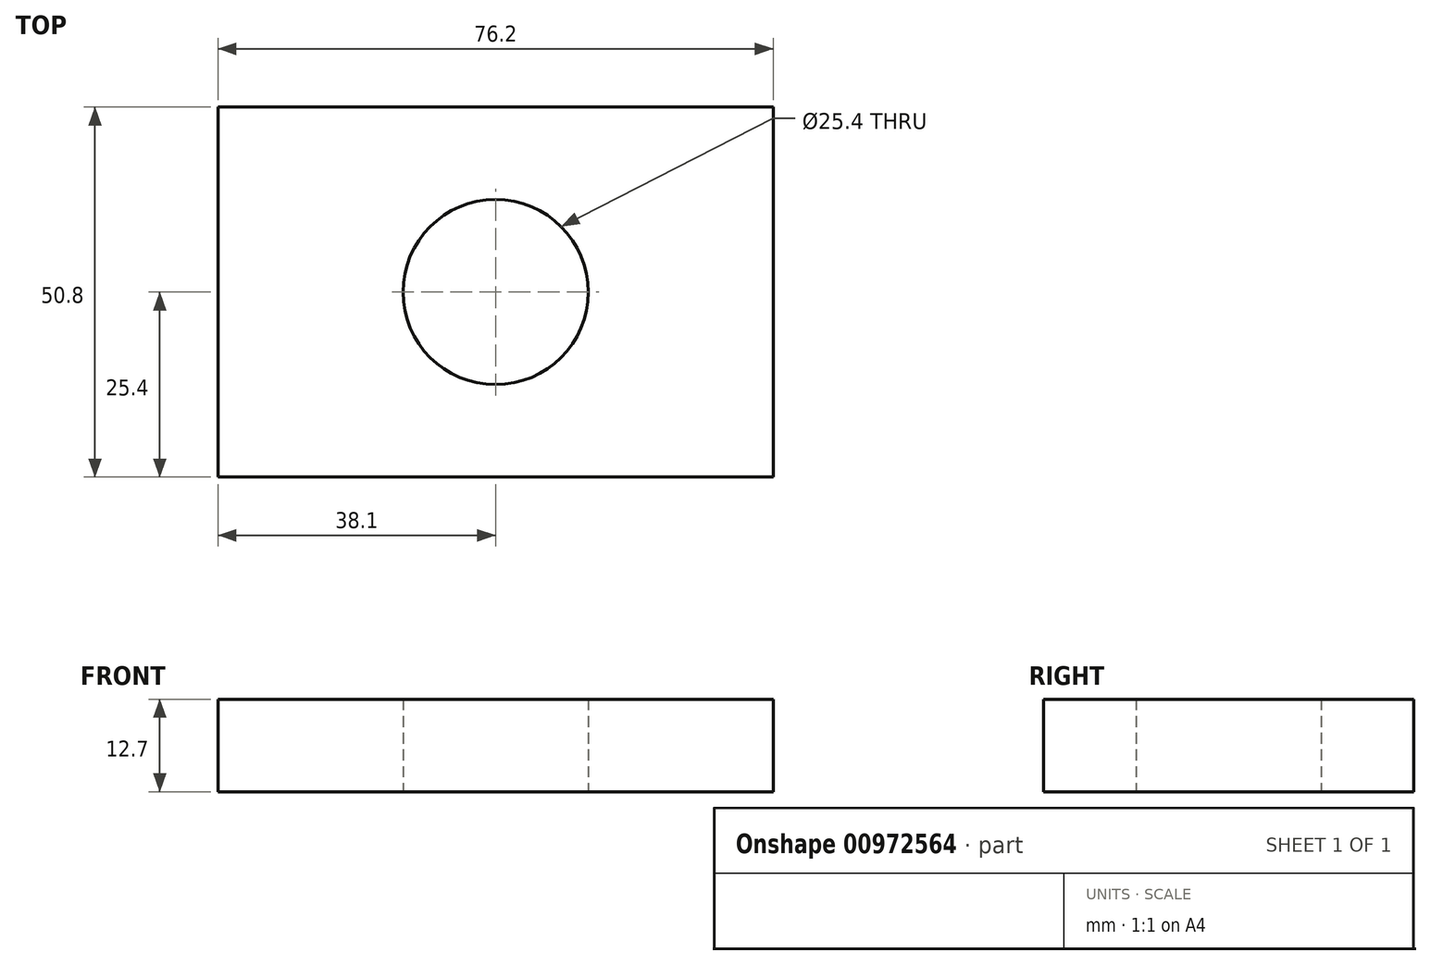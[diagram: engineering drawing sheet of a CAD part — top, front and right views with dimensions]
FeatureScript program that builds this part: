
annotation { "Feature Type Name" : "Feature", "Feature Type Description" : "" }
export const myFeature = defineFeature(function(context is Context, id is Id, definition is map)
    precondition{}
    {
        {
            var Q0;
            Q0=qCreatedBy(makeId("Top.planeOp"),FACE);
            var sketch = newSketch(context, id + "F0", { "sketchPlane" : qUnion([Q0])});
            skLineSegment(sketch, "E0.bottom", {"start": v(-38.1, -25.4) * mm, "end": v(38.1, -25.4) * mm});
            skLineSegment(sketch, "E0.top", {"start": v(-38.1, 25.4) * mm, "end": v(38.1, 25.4) * mm});
            skLineSegment(sketch, "E0.left", {"start": v(-38.1, -25.4) * mm, "end": v(-38.1, 25.4) * mm});
            skLineSegment(sketch, "E0.right", {"start": v(38.1, -25.4) * mm, "end": v(38.1, 25.4) * mm});
            skPoint(sketch, "E0.middle", {"position": v(0, 0) * mm});
            skCircle(sketch, "E1", {"center": v(0, 0) * mm, "radius": 12.7 * mm});
            skSolve(sketch);
        }
        {
            var Q0;
            Q0=makeQuery(id+"F0.imprint","IMPRINT",FACE,{"disambiguationData":[TD([[makeQuery(id+"F0.imprint","IMPRINT",EDGE,{"derivedFrom":sQuery(id+"F0.wireOp",EDGE,"E0.bottom")}),1.0]])]});
            extrude(context, id + "F1", {"entities" : qUnion([Q0]), "depth" : 12.7 * mm, "offsetDistance" : 25.4 * mm});
        }
    });
